# Revit family: Haworth_Tibas_Desk_Rectangular_AP_PRELIMINARY1
name_source: partatom
category: Furniture
units: mm (PartAtom-declared; Revit-internal decimal feet)

## family parameters
Always vertical = Yes
Cut with Voids When Loaded = No
OmniClass Number = 23.40.70.14.64.11
OmniClass Title = Office Furniture
Room Calculation Point = No
Shared = No
Work Plane-Based = No

## types (5) — shared parameters
Assembly Code = E2020200
Cable Tray = Yes
Cable Tray Finish = Haworth _ Paint _ Metallic Silver
Description = Haworth - Tibas - Desk - Rectangular
Manufacturer = Haworth
Model = SYTBRDXXXX
Product URL = https://www.haworth.com
Revision Number = 1
Size = Verify Final Dim.w/ Haworth
Trim Finish = Haworth _ Polymer _ Undecided
URL = https://www.haworth.com
Warranty = http://www.haworth.com
Worksurface Depth = 600, 700, 750, 800 mm
Worksurface Width = 1200, 1400, 1500, 1600, 1800 mm

## per-type parameters (varying)
| type | Accessory Kit | Actual Depth | Actual Height | Actual Width | Cable Tray Width | Flip Top Cable Outlet | Flip Top Width | Leg Height | No Accessory Kit | Round Cable Outlet |
| 1200w | Yes | 600 mm | 835 mm | 1200 mm | 700 mm | Yes | 200 mm  [stored 0.656168 ft] | 800 mm  [stored 2.62467 ft] | No | No |
| 1400w | Yes | 700 mm | 835 mm | 1400 mm | 900 mm | No | 200 mm  [stored 0.656168 ft] | 800 mm  [stored 2.62467 ft] | No | Yes |
| 1600w | Yes | 800 mm  [stored 2.62467 ft] | 740 mm  [stored 2.42782 ft] | 1600 mm | 1100 mm | Yes | 200 mm  [stored 0.656168 ft] | 705 mm  [stored 2.31299 ft] | No | No |
| 1800w | No | 800 mm  [stored 2.62467 ft] | 740 mm  [stored 2.42782 ft] | 1800 mm  [stored 5.90551 ft] | 1300 mm | No | 400 mm  [stored 1.31234 ft] | 705 mm  [stored 2.31299 ft] | Yes | No |
| 1500w | No | 750 mm  [stored 2.46063 ft] | 835 mm | 1500 mm  [stored 4.92126 ft] | 1000 mm | No | 200 mm  [stored 0.656168 ft] | 800 mm  [stored 2.62467 ft] | Yes | No |

note: [stored X ft] marks values corroborated as IEEE doubles in the binary element streams (Revit-internal decimal feet)

## geometry (parser evidence)
native form markers: Sweep x25
no freeform markers — native parametric forms only
